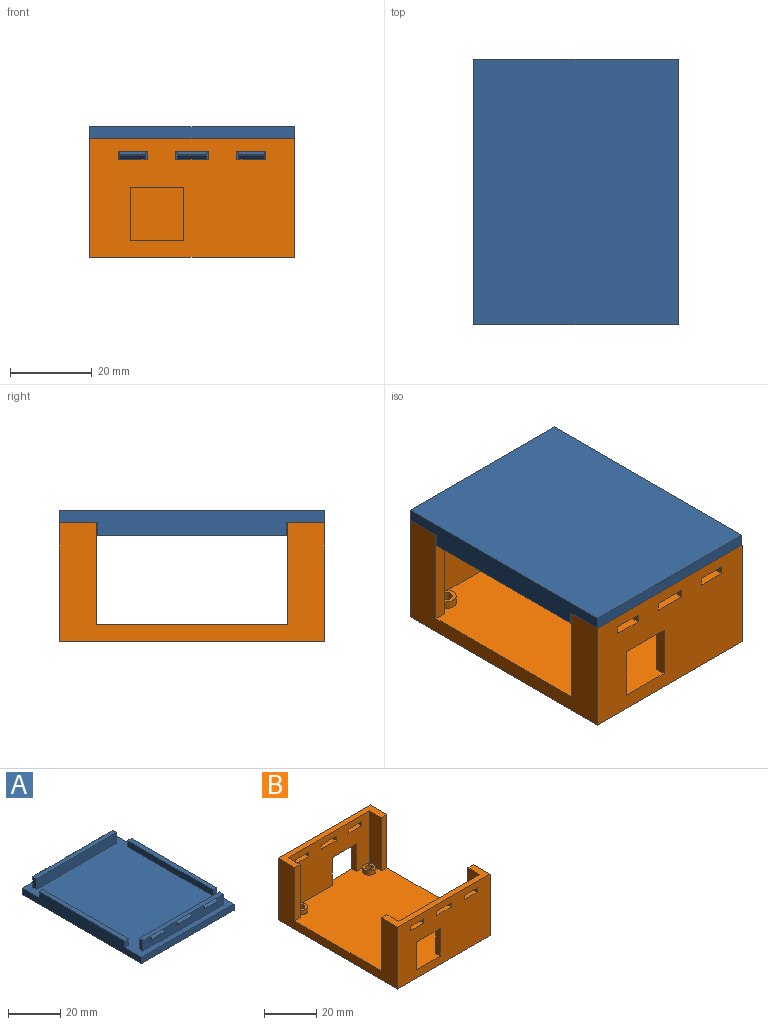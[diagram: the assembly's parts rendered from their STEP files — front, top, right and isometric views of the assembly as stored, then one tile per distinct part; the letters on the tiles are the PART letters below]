
ASSEMBLY  parts=2 mates=1
PART A: 54 faces, bbox 50x65x8 mm
  f0: plane 65x50mm, normal (0,0,1), area 2889.6mm2, adj f1,f2,f21,f22,f23,f24,f26,f27
  f1: plane 5x2mm, normal (-1,0,0), area 10mm2, adj f0,f26,f27,f29
  f2: plane 5x2mm, normal (1,0,0), area 10mm2, adj f0,f31,f32,f33
  f3: plane 6.5x1mm, normal (0,0.64,0.77), area 8.5mm2, adj f6,f29,f40,f44
  f4: plane 7.2x1mm, normal (0,0.64,0.77), area 9.4mm2, adj f7,f29,f42,f43
  f5: plane 6.5x1mm, normal (0,0.64,0.77), area 8.5mm2, adj f8,f29,f41,f45
  f6: plane 6.5x0.32mm, normal (0,1,0), area 2.1mm2, adj f3,f9,f40,f44
  f7: plane 7.2x0.32mm, normal (0,1,0), area 2.3mm2, adj f4,f10,f42,f43
  f8: plane 6.5x0.32mm, normal (0,1,0), area 2.1mm2, adj f5,f11,f41,f45
  f9: plane 6.5x1mm, normal (0,0.64,-0.77), area 8.5mm2, adj f6,f26,f40,f44
  f10: plane 7.2x1mm, normal (0,0.64,-0.77), area 9.4mm2, adj f7,f26,f42,f43
  f11: plane 6.5x1mm, normal (0,0.64,-0.77), area 8.5mm2, adj f8,f26,f41,f45
  f12: plane 6.5x1mm, normal (0,-0.64,0.77), area 8.5mm2, adj f18,f33,f37,f39
  f13: plane 7.2x1mm, normal (0,-0.64,0.77), area 9.4mm2, adj f19,f33,f36,f38
  f14: plane 6.5x1mm, normal (0,-0.64,0.77), area 8.5mm2, adj f20,f33,f34,f35
  f15: plane 6.5x1mm, normal (0,-0.64,-0.77), area 8.5mm2, adj f18,f31,f37,f39
  f16: plane 7.2x1mm, normal (0,-0.64,-0.77), area 9.4mm2, adj f19,f31,f36,f38
  f17: plane 6.5x1mm, normal (0,-0.64,-0.77), area 8.5mm2, adj f20,f31,f34,f35
  f18: plane 6.5x0.32mm, normal (0,-1,0), area 2.1mm2, adj f12,f15,f37,f39
  f19: plane 7.2x0.32mm, normal (0,-1,0), area 2.3mm2, adj f13,f16,f36,f38
  f20: plane 6.5x0.32mm, normal (0,-1,0), area 2.1mm2, adj f14,f17,f34,f35
  f21: plane 65x6mm, normal (-1,0,0), area 334.5mm2, adj f0,f22,f24,f25,f46,f47,f49
  f22: plane 50x3mm, normal (0,-1,0), area 150mm2, adj f0,f21,f23,f25
  f23: plane 65x6mm, normal (1,0,0), area 334.5mm2, adj f0,f22,f24,f25,f50,f52,f53
  f24: plane 50x3mm, normal (0,1,0), area 150mm2, adj f0,f21,f23,f25
  f25: plane 65x50mm, normal (0,0,-1), area 3250mm2, adj f21,f22,f23,f24
  f26: plane 43.6x5mm, normal (0,1,0), area 177.6mm2, adj f0,f1,f9,f10,f11,f28,f29,f40
  f27: plane 43.6x5mm, normal (0,-1,0), area 218mm2, adj f0,f1,f28,f29
  f28: plane 5x2mm, normal (1,0,0), area 10mm2, adj f0,f26,f27,f29
  f29: plane 43.6x2mm, normal (0,0,1), area 87.2mm2, adj f1,f3,f4,f5,f26,f27,f28
  f30: plane 5x2mm, normal (-1,0,0), area 10mm2, adj f0,f31,f32,f33
  f31: plane 43.6x5mm, normal (0,-1,0), area 177.6mm2, adj f0,f2,f15,f16,f17,f30,f33,f34
  f32: plane 43.6x5mm, normal (0,1,0), area 218mm2, adj f0,f2,f30,f33
  f33: plane 43.6x2mm, normal (0,0,1), area 87.2mm2, adj f2,f12,f13,f14,f30,f31,f32
  f34: plane 2x1mm, normal (-1,0,0), area 1.2mm2, adj f14,f17,f20,f31
  f35: plane 2x1mm, normal (1,0,0), area 1.2mm2, adj f14,f17,f20,f31
  f36: plane 2x1mm, normal (-1,0,0), area 1.2mm2, adj f13,f16,f19,f31
  f37: plane 2x1mm, normal (1,0,0), area 1.2mm2, adj f12,f15,f18,f31
  f38: plane 2x1mm, normal (1,0,0), area 1.2mm2, adj f13,f16,f19,f31
  f39: plane 2x1mm, normal (-1,0,0), area 1.2mm2, adj f12,f15,f18,f31
  f40: plane 2x1mm, normal (1,0,0), area 1.2mm2, adj f3,f6,f9,f26
  f41: plane 2x1mm, normal (1,0,0), area 1.2mm2, adj f5,f8,f11,f26
  f42: plane 2x1mm, normal (-1,0,0), area 1.2mm2, adj f4,f7,f10,f26
  f43: plane 2x1mm, normal (1,0,0), area 1.2mm2, adj f4,f7,f10,f26
  f44: plane 2x1mm, normal (-1,0,0), area 1.2mm2, adj f3,f6,f9,f26
  f45: plane 2x1mm, normal (-1,0,0), area 1.2mm2, adj f5,f8,f11,f26
  f46: plane 3x2mm, normal (0,1,0), area 6mm2, adj f0,f21,f48,f49
  f47: plane 3x2mm, normal (0,-1,0), area 6mm2, adj f0,f21,f48,f49
  f48: plane 46.5x3mm, normal (1,0,0), area 139.5mm2, adj f0,f46,f47,f49
  f49: plane 46.5x2mm, normal (0,0,1), area 93mm2, adj f21,f46,f47,f48
  f50: plane 3x2mm, normal (0,1,0), area 6mm2, adj f0,f23,f51,f53
  f51: plane 46.5x3mm, normal (-1,0,0), area 139.5mm2, adj f0,f50,f52,f53
  f52: plane 3x2mm, normal (0,-1,0), area 6mm2, adj f0,f23,f51,f53
  f53: plane 46.5x2mm, normal (0,0,1), area 93mm2, adj f23,f50,f51,f52
PART B: 60 faces, bbox 50x65x29 mm
  f0: plane 50x29mm, normal (0,1,0), area 1237mm2, adj f4,f5,f6,f7,f17,f21,f22,f23
  f1: plane 44x25mm, normal (0,-1,0), area 887mm2, adj f4,f14,f15,f17,f21,f22,f23,f48
  f2: plane 50x29mm, normal (0,-1,0), area 1237mm2, adj f4,f5,f6,f7,f12,f18,f19,f20
  f3: plane 44x25mm, normal (0,1,0), area 887mm2, adj f4,f8,f11,f12,f18,f19,f20,f36
  f4: plane 65x50mm, normal (0,0,1), area 2908.5mm2, adj f0,f1,f2,f3,f5,f6,f8,f9
  f5: plane 65x29mm, normal (-1,0,0), area 710mm2, adj f0,f2,f4,f7,f9,f12,f13,f17
  f6: plane 65x29mm, normal (1,0,0), area 710mm2, adj f0,f2,f4,f7,f10,f12,f16,f17
  f7: plane 65x50mm, normal (0,0,-1), area 3221.7mm2, adj f0,f2,f5,f6,f24,f25,f26,f27
  f8: plane 25x6.5mm, normal (1,0,0), area 162.5mm2, adj f3,f4,f9,f12
  f9: plane 25x3mm, normal (0,1,0), area 75mm2, adj f4,f5,f8,f12
  f10: plane 25x3mm, normal (0,1,0), area 75mm2, adj f4,f6,f11,f12
  f11: plane 25x6.5mm, normal (-1,0,0), area 162.5mm2, adj f3,f4,f10,f12
  f12: plane 50x9mm, normal (0,0,1), area 164mm2, adj f2,f3,f5,f6,f8,f9,f10,f11
  f13: plane 25x3mm, normal (0,-1,0), area 75mm2, adj f4,f5,f14,f17
  f14: plane 25x6.5mm, normal (1,0,0), area 162.5mm2, adj f1,f4,f13,f17
  f15: plane 25x6.5mm, normal (-1,0,0), area 162.5mm2, adj f1,f4,f16,f17
  f16: plane 25x3mm, normal (0,-1,0), area 75mm2, adj f4,f6,f15,f17
  f17: plane 50x9mm, normal (0,0,1), area 164mm2, adj f0,f1,f5,f6,f13,f14,f15,f16
  f18: plane 13x2.5mm, normal (1,0,0), area 32.5mm2, adj f2,f3,f4,f20
  f19: plane 13x2.5mm, normal (-1,0,0), area 32.5mm2, adj f2,f3,f4,f20
  f20: plane 13x2.5mm, normal (0,0,-1), area 32.5mm2, adj f2,f3,f18,f19
  f21: plane 13x2.5mm, normal (-1,0,0), area 32.5mm2, adj f0,f1,f4,f23
  f22: plane 13x2.5mm, normal (1,0,0), area 32.5mm2, adj f0,f1,f4,f23
  f23: plane 13x2.5mm, normal (0,0,-1), area 32.5mm2, adj f0,f1,f21,f22
  f24: cylinder r=1.5mm len=6mm, axis (0,0,1), area 56.5mm2, adj f7,f29
  f25: cylinder r=1.5mm len=6mm, axis (0,0,1), area 56.5mm2, adj f7,f31
  f26: cylinder r=1.5mm len=6mm, axis (0,0,1), area 56.5mm2, adj f7,f35
  f27: cylinder r=1.5mm len=6mm, axis (0,0,1), area 56.5mm2, adj f7,f33
  f28: cylinder r=2.5mm len=5mm, axis (0,0,-1), area 31.4mm2, adj f4,f29
  f29: plane 5x5mm, normal (0,0,1), area 12.6mm2, adj f24,f28
  f30: cylinder r=2.5mm len=5mm, axis (0,0,-1), area 31.4mm2, adj f4,f31
  f31: plane 5x5mm, normal (0,0,1), area 12.6mm2, adj f25,f30
  f32: cylinder r=2.5mm len=5mm, axis (0,0,-1), area 31.4mm2, adj f4,f33
  f33: plane 5x5mm, normal (0,0,1), area 12.6mm2, adj f27,f32
  f34: cylinder r=2.5mm len=5mm, axis (0,0,-1), area 31.4mm2, adj f4,f35
  f35: plane 5x5mm, normal (0,0,1), area 12.6mm2, adj f26,f34
  f36: plane 2.5x2mm, normal (-1,0,0), area 5mm2, adj f2,f3,f37,f39
  f37: plane 8x2.5mm, normal (0,0,1), area 20mm2, adj f2,f3,f36,f38
  f38: plane 2.5x2mm, normal (1,0,0), area 5mm2, adj f2,f3,f37,f39
  f39: plane 8x2.5mm, normal (0,0,-1), area 20mm2, adj f2,f3,f36,f38
  f40: plane 2.5x2mm, normal (-1,0,0), area 5mm2, adj f2,f3,f41,f43
  f41: plane 7x2.5mm, normal (0,0,1), area 17.5mm2, adj f2,f3,f40,f42
  f42: plane 2.5x2mm, normal (1,0,0), area 5mm2, adj f2,f3,f41,f43
  f43: plane 7x2.5mm, normal (0,0,-1), area 17.5mm2, adj f2,f3,f40,f42
  f44: plane 2.5x2mm, normal (-1,0,0), area 5mm2, adj f2,f3,f45,f47
  f45: plane 7x2.5mm, normal (0,0,1), area 17.5mm2, adj f2,f3,f44,f46
  f46: plane 2.5x2mm, normal (1,0,0), area 5mm2, adj f2,f3,f45,f47
  f47: plane 7x2.5mm, normal (0,0,-1), area 17.5mm2, adj f2,f3,f44,f46
  f48: plane 8x2.5mm, normal (0,0,-1), area 20mm2, adj f0,f1,f49,f51
  f49: plane 2.5x2mm, normal (1,0,0), area 5mm2, adj f0,f1,f48,f50
  f50: plane 8x2.5mm, normal (0,0,1), area 20mm2, adj f0,f1,f49,f51
  f51: plane 2.5x2mm, normal (-1,0,0), area 5mm2, adj f0,f1,f48,f50
  f52: plane 7x2.5mm, normal (0,0,-1), area 17.5mm2, adj f0,f1,f53,f55
  f53: plane 2.5x2mm, normal (1,0,0), area 5mm2, adj f0,f1,f52,f54
  f54: plane 7x2.5mm, normal (0,0,1), area 17.5mm2, adj f0,f1,f53,f55
  f55: plane 2.5x2mm, normal (-1,0,0), area 5mm2, adj f0,f1,f52,f54
  f56: plane 7x2.5mm, normal (0,0,-1), area 17.5mm2, adj f0,f1,f57,f59
  f57: plane 2.5x2mm, normal (1,0,0), area 5mm2, adj f0,f1,f56,f58
  f58: plane 7x2.5mm, normal (0,0,1), area 17.5mm2, adj f0,f1,f57,f59
  f59: plane 2.5x2mm, normal (-1,0,0), area 5mm2, adj f0,f1,f56,f58
PLACE A rot(axis=(1,0,0),180deg) t=(-4.04,65.83,59.85)mm
PLACE B t=(-4.04,0.83,27.85)mm
MATE fastened A.f0 <-> B.f17  axis (0,0,-1) through (20.96,65.83,56.85)mm
